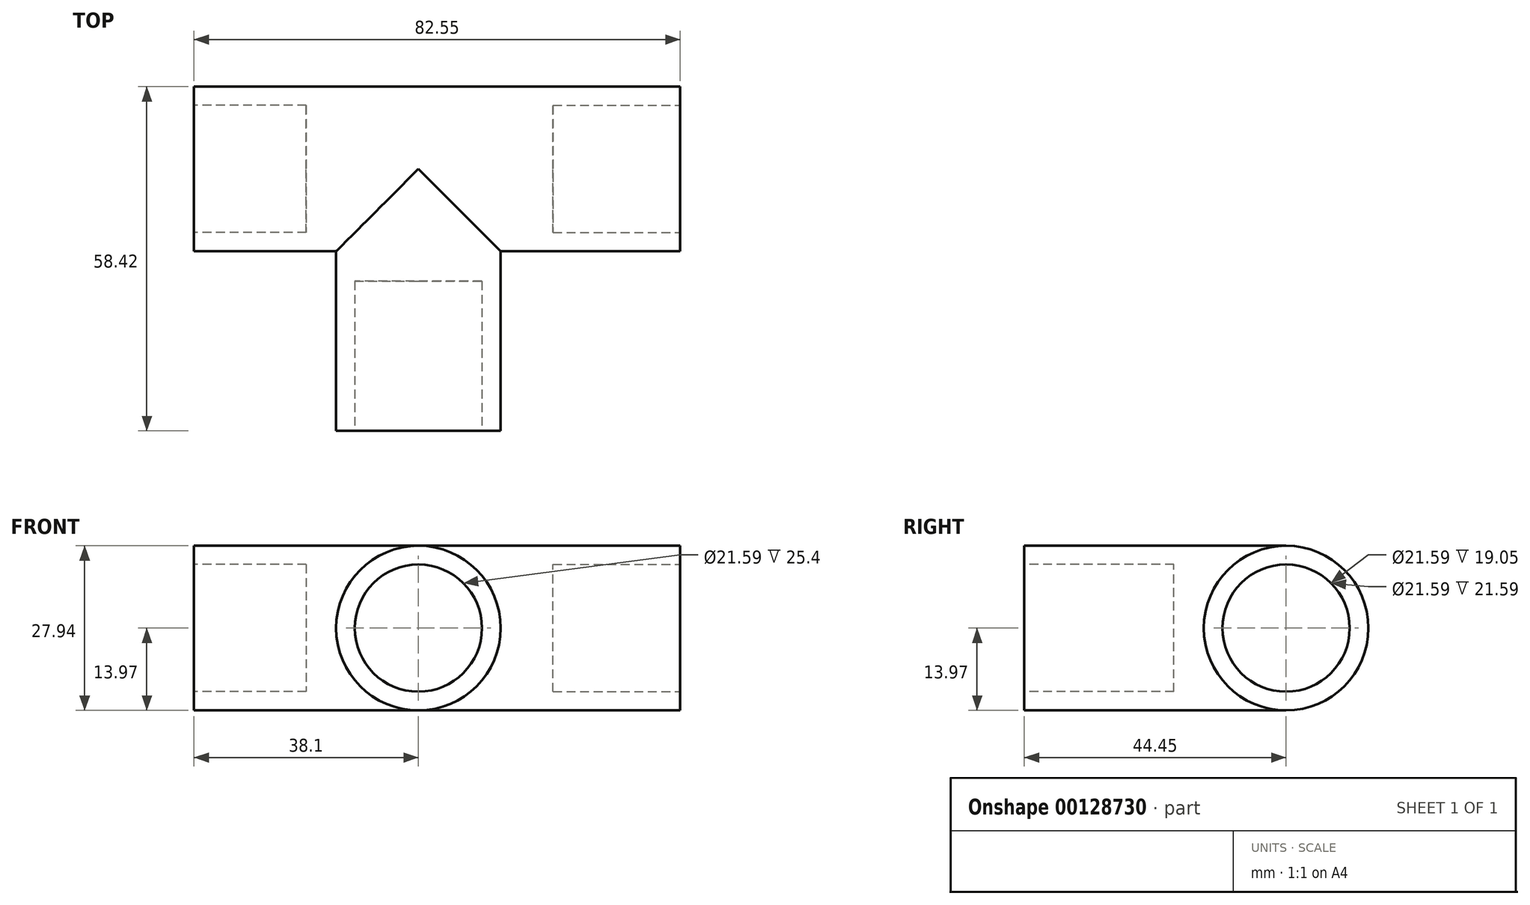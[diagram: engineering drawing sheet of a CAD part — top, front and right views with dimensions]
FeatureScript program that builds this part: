
annotation { "Feature Type Name" : "Feature", "Feature Type Description" : "" }
export const myFeature = defineFeature(function(context is Context, id is Id, definition is map)
    precondition{}
    {
        {
            var Q0;
            Q0=qCreatedBy(makeId("Right.planeOp"),FACE);
            var sketch = newSketch(context, id + "F0", { "sketchPlane" : qUnion([Q0])});
            skCircle(sketch, "E0", {"center": v(0, 0) * mm, "radius": 13.97 * mm});
            skSolve(sketch);
        }
        {
            var Q0;
            Q0=makeQuery(id+"F0.imprint","IMPRINT",FACE,{"disambiguationData":[TD([[makeQuery(id+"F0.imprint","IMPRINT",EDGE,{"derivedFrom":sQuery(id+"F0.wireOp",EDGE,"E0")}),1.0]])]});
            extrude(context, id + "F1", {"entities" : qUnion([Q0]), "depth" : 44.45 * mm});
        }
        {
            var Q0;
            Q0=makeQuery(id+"F1.opExtrude","CAP_FACE",FACE,{"disambiguationData":[OSD([sQuery(id+"F0.wireOp",EDGE,"E0")])],"isStart":true});
            var sketch = newSketch(context, id + "F2", { "sketchPlane" : qUnion([Q0])});
            skSolve(sketch);
        }
        {
            var Q0;
            Q0=makeQuery(id+"F2.imprint","IMPRINT",FACE,{"disambiguationData":[TD([[makeQuery(id+"F2.imprint","IMPRINT",EDGE,{"derivedFrom":makeQuery(id+"F1.opExtrude","CAP_EDGE",EDGE,{"disambiguationData":[OSD([sQuery(id+"F0.wireOp",EDGE,"E0")])],"isStart":true})}),-1.0]])]});
            extrude(context, id + "F3", {"entities" : qUnion([Q0]), "operationType" : NewBodyOperationType.ADD, "depth" : 38.1 * mm});
        }
        {
            var Q0;
            Q0=qCreatedBy(makeId("Front.planeOp"),FACE);
            var sketch = newSketch(context, id + "F4", { "sketchPlane" : qUnion([Q0])});
            skCircle(sketch, "E1", {"center": v(0, 0) * mm, "radius": 13.97 * mm});
            skSolve(sketch);
        }
        {
            var Q0;
            Q0 = qSketchRegion(id + "F4", true);
            var Q1;
            Q1 = qSketchRegion(id + "F6", true);
            extrude(context, id + "F5", {"entities" : qUnion([Q0, Q1]), "operationType" : NewBodyOperationType.ADD, "depth" : 44.45 * mm});
        }
        {
            var Q0;
            Q0=makeQuery(id+"F3.opExtrude","CAP_FACE",FACE,{"disambiguationData":[OSD([sQuery(id+"F0.wireOp",EDGE,"E0")])],"isStart":false});
            var sketch = newSketch(context, id + "F6", { "sketchPlane" : qUnion([Q0])});
            skCircle(sketch, "E2", {"center": v(0, 0) * mm, "radius": 10.8 * mm});
            skSolve(sketch);
        }
        {
            var Q0;
            Q0 = qSketchRegion(id + "F6", true);
            extrude(context, id + "F7", {"entities" : qUnion([Q0]), "operationType" : NewBodyOperationType.REMOVE, "oppositeDirection" : true, "depth" : 19.05 * mm});
        }
        {
            var Q0;
            Q0=makeQuery(id+"F1.opExtrude","CAP_FACE",FACE,{"disambiguationData":[OSD([sQuery(id+"F0.wireOp",EDGE,"E0")])],"isStart":false});
            var sketch = newSketch(context, id + "F8", { "sketchPlane" : qUnion([Q0])});
            skCircle(sketch, "E3", {"center": v(0, 0) * mm, "radius": 10.8 * mm});
            skSolve(sketch);
        }
        {
            var Q0;
            Q0=makeQuery(id+"F8.imprint","IMPRINT",FACE,{"disambiguationData":[TD([[makeQuery(id+"F8.imprint","IMPRINT",EDGE,{"derivedFrom":sQuery(id+"F8.wireOp",EDGE,"E3")}),1.0]])]});
            extrude(context, id + "F9", {"entities" : qUnion([Q0]), "operationType" : NewBodyOperationType.REMOVE, "oppositeDirection" : true, "depth" : 21.59 * mm});
        }
        {
            var Q0;
            Q0=makeQuery(id+"F5.opExtrude","CAP_FACE",FACE,{"disambiguationData":[OSD([sQuery(id+"F4.wireOp",EDGE,"E1")])],"isStart":false});
            var sketch = newSketch(context, id + "F10", { "sketchPlane" : qUnion([Q0])});
            skCircle(sketch, "E4", {"center": v(0, 0) * mm, "radius": 10.8 * mm});
            skSolve(sketch);
        }
        {
            var Q0;
            Q0=makeQuery(id+"F10.imprint","IMPRINT",FACE,{"disambiguationData":[TD([[makeQuery(id+"F10.imprint","IMPRINT",EDGE,{"derivedFrom":sQuery(id+"F10.wireOp",EDGE,"E4")}),1.0]])]});
            extrude(context, id + "F11", {"entities" : qUnion([Q0]), "operationType" : NewBodyOperationType.REMOVE, "oppositeDirection" : true, "depth" : 25.4 * mm});
        }
    });
